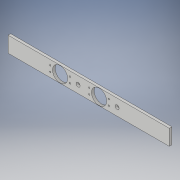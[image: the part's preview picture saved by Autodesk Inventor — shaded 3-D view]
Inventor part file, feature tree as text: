
AUTODESK INVENTOR PART (.ipt)
format: ipt  version: 2017 (Build 210142000, 142)  size: 133,632 bytes
history: native  units: in
note: dims shown in document units (in); Inventor stores cm internally (conversion verified against a paired STEP export)
features: extrude x3, sketch x1, hole x1, chamfer x1
ambient origin geometry x8: Origin, YZ Plane, XZ Plane, XY Plane, X Axis, Y Axis, Z Axis, Center Point
bodies: Solid1 (feature_tree)
feature tree (6):
  sketch  "Sketch1"  dims[d0=1.5in d1=15.5in d3=1.46in d5=1.46in d6=0.25in d7=0.0in d10=0.14in d11=0.14in d12=0.14in d13=0.75in d14=0.375in d15=0.25in d16=0.5635in d17=1.0in d18=0.8108in d19=0.125in d20=0.125in d21=45.0deg d24=0.276in d28=0.138in d29=0.138in d30=0.138in d31=0.945in d38=0.138in d39=0.138in d40=0.138in d41=0.138in d42=0.25in d43=0.0in d44=0.25in d45=0.0in]
  extrude  "Extrusion1"  Depth=15.5in
  hole  "Hole1"  [1 undecoded]
  chamfer  "Chamfer1"  Distance=1.46in
  extrude  "Extrusion2"  Depth=0.25in TaperAngle=0.0deg
  extrude  "Extrusion3"  Depth=0.25in
note: 1 required parameter value undecoded (feature->parameter linkage not recoverable at this tier; creation-order binding heuristic only, values carry confidence <= 0.55)
